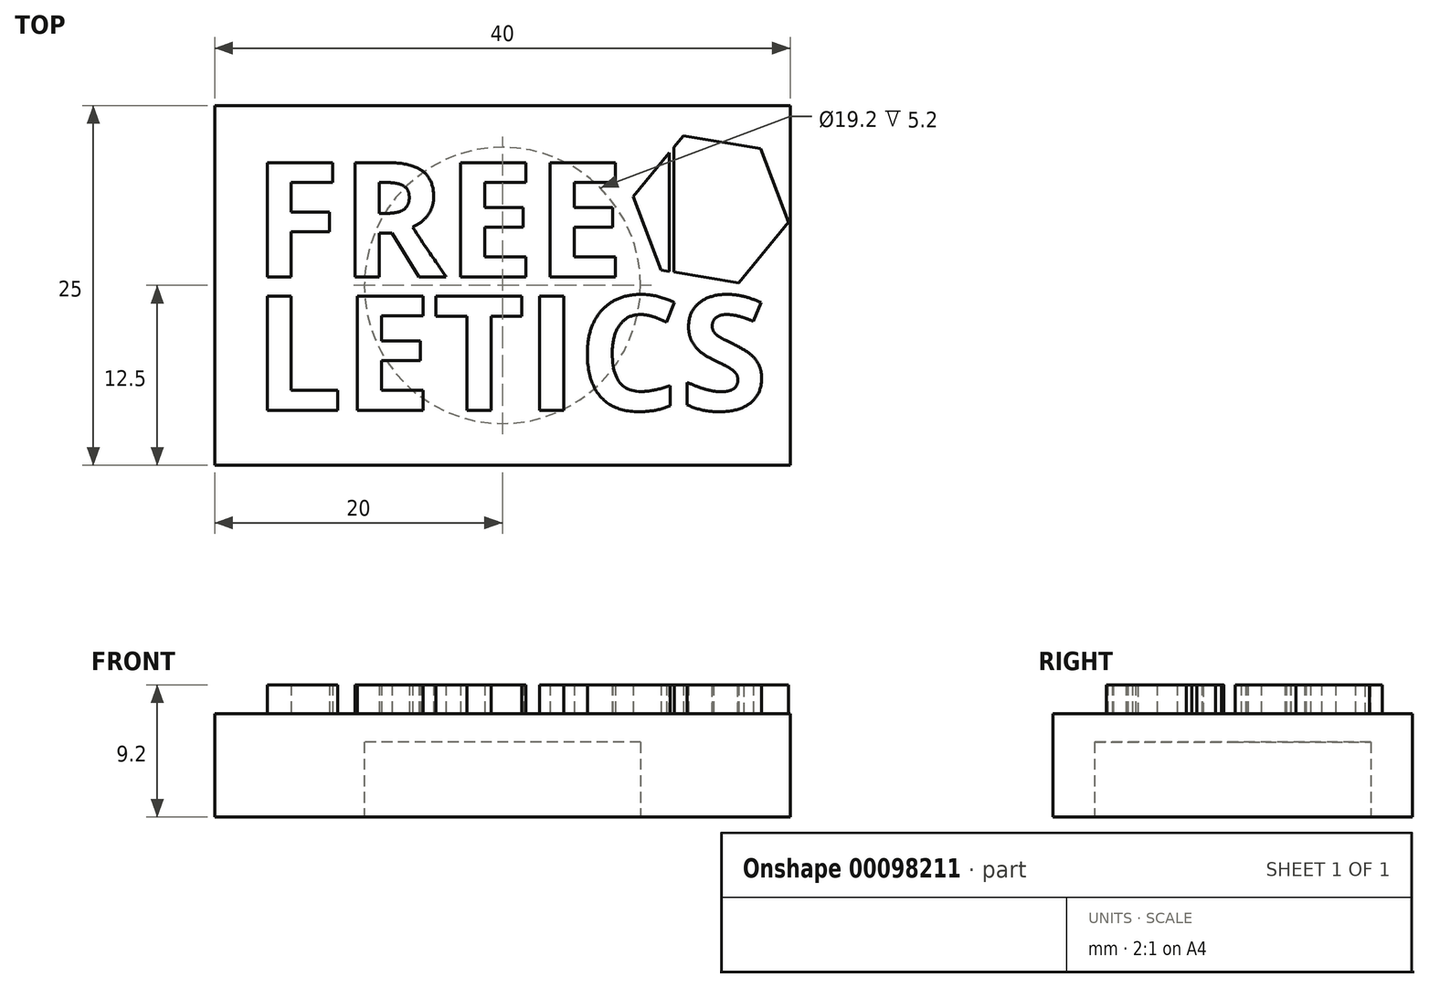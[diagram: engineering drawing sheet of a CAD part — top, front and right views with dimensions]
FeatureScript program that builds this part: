
annotation { "Feature Type Name" : "Feature", "Feature Type Description" : "" }
export const myFeature = defineFeature(function(context is Context, id is Id, definition is map)
    precondition{}
    {
        {
            var Q0;
            Q0=qCreatedBy(makeId("Top.planeOp"),FACE);
            var sketch = newSketch(context, id + "F0", { "sketchPlane" : qUnion([Q0])});
            skCircle(sketch, "E0", {"center": v(0, 0) * mm, "radius": 9.6 * mm});
            skCircle(sketch, "E1.0", {"center": v(0, 0) * mm, "radius": 11.6 * mm});
            skSolve(sketch);
        }
        {
            var Q0;
            Q0=qSketchRegion(id+"F0",true);
            extrude(context, id + "F1", {"entities" : qUnion([Q0]), "depth" : 5.2 * mm});
        }
        {
            var Q0;
            Q0=makeQuery(id+"F1.opExtrude","CAP_FACE",FACE,{"disambiguationData":[OSD([sQuery(id+"F0.wireOp",EDGE,"E0"),sQuery(id+"F0.wireOp",EDGE,"E1.0")])],"isStart":false});
            var sketch = newSketch(context, id + "F2", { "sketchPlane" : qUnion([Q0])});
            skSolve(sketch);
        }
        {
            var Q0;
            Q0=makeQuery(id+"F2.imprint","IMPRINT",FACE,{"disambiguationData":[TD([[makeQuery(id+"F2.imprint","IMPRINT",EDGE,{"derivedFrom":makeQuery(id+"F1.opExtrude","CAP_EDGE",EDGE,{"disambiguationData":[OSD([sQuery(id+"F0.wireOp",EDGE,"E0")])],"isStart":false})}),1.0]])]});
            var Q1;
            Q1=makeQuery(id+"F2.imprint","IMPRINT",FACE,{"disambiguationData":[TD([[makeQuery(id+"F2.imprint","IMPRINT",EDGE,{"derivedFrom":makeQuery(id+"F1.opExtrude","CAP_EDGE",EDGE,{"disambiguationData":[OSD([sQuery(id+"F0.wireOp",EDGE,"E0")])],"isStart":false})}),-1.0]])]});
            extrude(context, id + "F3", {"entities" : qUnion([Q0, Q1]), "operationType" : NewBodyOperationType.ADD, "depth" : 2 * mm});
        }
        {
            var Q0;
            Q0=makeQuery(id+"F3.opExtrude","CAP_FACE",FACE,{"disambiguationData":[OSD([sQuery(id+"F0.wireOp",EDGE,"E1.0")])],"isStart":false});
            var sketch = newSketch(context, id + "F4", { "sketchPlane" : qUnion([Q0])});
            skLineSegment(sketch, "E2.bottom", {"start": v(-20, 12.5) * mm, "end": v(20, 12.5) * mm});
            skLineSegment(sketch, "E2.top", {"start": v(-20, -12.5) * mm, "end": v(20, -12.5) * mm});
            skLineSegment(sketch, "E2.left", {"start": v(-20, 12.5) * mm, "end": v(-20, -12.5) * mm});
            skLineSegment(sketch, "E2.right", {"start": v(20, 12.5) * mm, "end": v(20, -12.5) * mm});
            skPoint(sketch, "E2.middle", {"position": v(0, 0) * mm});
            skSolve(sketch);
        }
        {
            var Q0;
            Q0=makeQuery(id+"F4.imprint","IMPRINT",FACE,{"disambiguationData":[TD([[makeQuery(id+"F4.imprint","IMPRINT",EDGE,{"derivedFrom":sQuery(id+"F4.wireOp",EDGE,"E2.bottom")}),-1.0]])]});
            extrude(context, id + "F5", {"entities" : qUnion([Q0]), "operationType" : NewBodyOperationType.ADD, "oppositeDirection" : true, "depth" : 7.2 * mm});
        }
        {
            var Q0;
            {var subQ0=sQuery(id+"F0.wireOp",EDGE,"E1.0");Q0=makeQuery(id+"F5.boolean.opBoolean","MERGE",FACE,{"derivedFrom":[makeQuery(id+"F3.opExtrude","CAP_FACE",FACE,{"disambiguationData":[OSD([subQ0])],"isStart":false}),makeQuery(id+"F5.opExtrude","CAP_FACE",FACE,{"disambiguationData":[OSD([subQ0,sQuery(id+"F4.wireOp",EDGE,"E2.bottom"),sQuery(id+"F4.wireOp",EDGE,"E2.top"),sQuery(id+"F4.wireOp",EDGE,"E2.left"),sQuery(id+"F4.wireOp",EDGE,"E2.right")])],"isStart":true})]});}
            var sketch = newSketch(context, id + "F6", { "sketchPlane" : qUnion([Q0])});
            skText(sketch, "E3", { "text": "FREE", "fontName": "OpenSans-Bold.ttf"});
            skText(sketch, "E4", { "text": "LETICS", "fontName": "OpenSans-Bold.ttf"});
            const initialGuessF6  = {"E3": [-0.01736, 0.0006, 1, 0, 0.008], "E4": [-0.01736, -0.00867, 1, 0, 0.008]};
            skSetInitialGuess(sketch, initialGuessF6);
            skSolve(sketch);
        }
        {
            var Q0;
            Q0 = qSketchRegion(id + "F6", true);
            extrude(context, id + "F7", {"entities" : qUnion([Q0]), "operationType" : NewBodyOperationType.ADD, "depth" : 2 * mm});
        }
        {
            var Q0;
            {var subQ0=sQuery(id+"F4.wireOp",EDGE,"E2.right");var subQ1=sQuery(id+"F4.wireOp",EDGE,"E2.top");var subQ8=sQuery(id+"F4.wireOp",EDGE,"E2.left");var subQ10=sQuery(id+"F4.wireOp",EDGE,"E2.bottom");var subQ32=sQuery(id+"F0.wireOp",EDGE,"E1.0");Q0=makeQuery(id+"F7.boolean.opBoolean","SPLIT",FACE,{"disambiguationData":[TD([makeQuery(id+"F5.opExtrude","SWEPT_FACE",FACE,{"disambiguationData":[OSD([subQ10])]})])],"derivedFrom":makeQuery(id+"F5.boolean.opBoolean","MERGE",FACE,{"derivedFrom":[makeQuery(id+"F3.opExtrude","CAP_FACE",FACE,{"disambiguationData":[OSD([subQ32])],"isStart":false}),makeQuery(id+"F5.opExtrude","CAP_FACE",FACE,{"disambiguationData":[OSD([subQ32,subQ10,subQ1,subQ8,subQ0])],"isStart":true})]})});}
            var sketch = newSketch(context, id + "F8", { "sketchPlane" : qUnion([Q0])});
            skCircle(sketch, "E5.cCircle", {"center": v(14.49, 5.29) * mm, "radius": 4.73 * mm, "construction": true});
            skLineSegment(sketch, "E5.0", {"start": v(9.1, 6.18) * mm, "end": v(12.57, 10.4) * mm});
            skLineSegment(sketch, "E5.1", {"start": v(12.57, 10.4) * mm, "end": v(17.96, 9.51) * mm});
            skLineSegment(sketch, "E5.2", {"start": v(17.96, 9.51) * mm, "end": v(19.88, 4.4) * mm});
            skLineSegment(sketch, "E5.3", {"start": v(19.88, 4.4) * mm, "end": v(16.4, 0.17) * mm});
            skLineSegment(sketch, "E5.4", {"start": v(16.4, 0.17) * mm, "end": v(11.02, 1.07) * mm});
            skLineSegment(sketch, "E5.5", {"start": v(11.02, 1.07) * mm, "end": v(9.1, 6.18) * mm});
            skPoint(sketch, "E5.0.midPoint", {"position": v(10.83, 8.3) * mm});
            skSolve(sketch);
        }
        {
            var Q0;
            Q0 = qSketchRegion(id + "F8", true);
            extrude(context, id + "F9", {"entities" : qUnion([Q0]), "operationType" : NewBodyOperationType.ADD, "depth" : 2 * mm});
        }
        {
            var Q0;
            Q0=makeQuery(id+"F9.opExtrude","CAP_FACE",FACE,{"disambiguationData":[OSD([sQuery(id+"F8.wireOp",EDGE,"E5.0"),sQuery(id+"F8.wireOp",EDGE,"E5.1"),sQuery(id+"F8.wireOp",EDGE,"E5.2"),sQuery(id+"F8.wireOp",EDGE,"E5.3"),sQuery(id+"F8.wireOp",EDGE,"E5.4"),sQuery(id+"F8.wireOp",EDGE,"E5.5")])],"isStart":false});
            var sketch = newSketch(context, id + "F10", { "sketchPlane" : qUnion([Q0])});
            skLineSegment(sketch, "E6.bottom", {"start": v(11.6, 10.12) * mm, "end": v(11.9, 10.12) * mm});
            skLineSegment(sketch, "E6.top", {"start": v(11.6, 0) * mm, "end": v(11.9, 0) * mm});
            skLineSegment(sketch, "E6.left", {"start": v(11.6, 10.12) * mm, "end": v(11.6, 0) * mm});
            skLineSegment(sketch, "E6.right", {"start": v(11.9, 10.12) * mm, "end": v(11.9, 0) * mm});
            skSolve(sketch);
        }
        {
            var Q0;
            Q0 = qSketchRegion(id + "F10", true);
            extrude(context, id + "F11", {"entities" : qUnion([Q0]), "operationType" : NewBodyOperationType.REMOVE, "oppositeDirection" : true, "depth" : 2 * mm});
        }
    });
